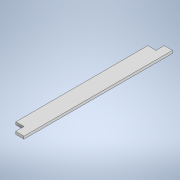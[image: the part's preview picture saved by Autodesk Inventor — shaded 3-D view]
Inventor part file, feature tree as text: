
AUTODESK INVENTOR PART (.ipt)
format: ipt  version: 2020 (Build 240168000, 168)  size: 106,496 bytes
history: native  units: mm
features: other x1, extrude x1, sketch x1
ambient origin geometry x8: Origin, YZ Plane, XZ Plane, XY Plane, X Axis, Y Axis, Z Axis, Center Point
bodies: Solid1 (feature_tree)
feature tree (3):
  other  "<userpath>\Documents\Development\paragon-printer\Paragon Printer Parameters.xlsx"
  extrude  "Extrusion1"  Depth=20.0mm
  sketch  "Sketch1"  dims[d0=360.0mm d1=20.0mm d2=20.0mm d3=20.0mm d4=20.0mm d5=40.0mm d6=6.35mm d7=0.0mm]
